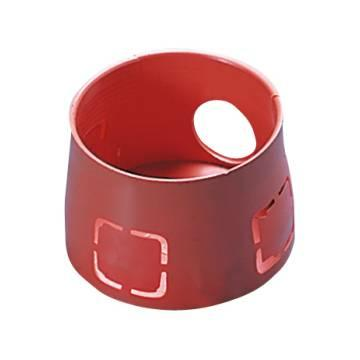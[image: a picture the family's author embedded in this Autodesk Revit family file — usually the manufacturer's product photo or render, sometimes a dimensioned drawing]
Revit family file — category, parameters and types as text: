
# Revit family: Building-FlushMountingEnclosures-GEWISS-24SC-BOXES_CONICAL
name_source: partatom
category: Attrezzatura elettrica
revit_build: Autodesk Revit 2016 (Build: 20161004_0715(x64)
units: mm (PartAtom-declared; Revit-internal decimal feet)

## family parameters
Condiviso = Sì
Configurazione quadro = Due colonne, circuiti in orizzontale
Host = Muro
Numero OmniClass = 23.80.30.14.24
Punto di calcolo locali = Sì
Quota connettore circolare = Usa diametro
Sempre verticale = Sì
Taglio con vuoti quando caricato = Sì
Tipo di parte = Pannello comandi
Titolo OmniClass = Junction Boxes

## types (1)
- GW24208 - Conical box D.65mm
    Catalogue = BUILDING
    Catalogue Range = 24SC
    Characteristics = Halogen free
    Description: = Conical
    Descrizione = CONICAL F.M.BOX D.65X41
    Dimensions (mm) = Ã˜ 60 x 46
    EAN code = 8011564016729
    Electrocod = 0210
    For walls = Masonry
    Glow Wire Test = 650°C
    IDF = f1faed0c-124c-4668-85a6-919ed2aaf81b
    IDT = 949ec92d-8c98-491b-b93a-f1d6dc8379db
    Immagine tipo = GW24208.jpg
    Installation = Flush mounting enclosures
    Modello = GW24208
    Operating temperature = -15 ÷ +60°C
    Produttore = GEWISS S.p.A.
    SEO = Box
    Technical sheet = https://www.gewiss.com
    Thermo-pressure with ball = 70
    URL = https://www.gewiss.com
    Version file RFA = 19.0

note: source unit labels omitted for Thermo-pressure with ball — the stored unit's dimension contradicts the parameter name (converter mislabeling)
